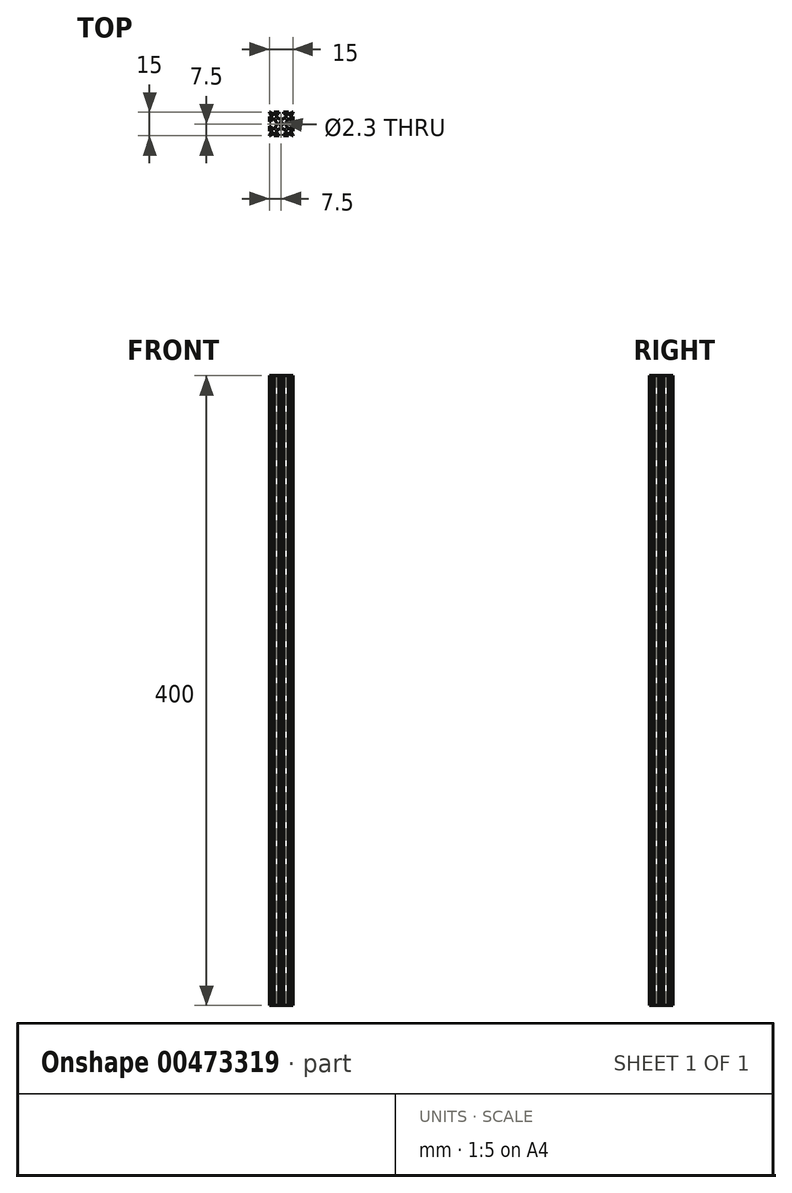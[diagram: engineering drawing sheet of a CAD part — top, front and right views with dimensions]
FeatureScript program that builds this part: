
annotation { "Feature Type Name" : "Feature", "Feature Type Description" : "" }
export const myFeature = defineFeature(function(context is Context, id is Id, definition is map)
    precondition{}
    {
        {
            var Q0;
            Q0=qCreatedBy(makeId("Top.planeOp"),FACE);
            var sketch = newSketch(context, id + "F0", { "sketchPlane" : qUnion([Q0])});
            skLineSegment(sketch, "E0", {"start": v(0, 0) * mm, "end": v(-7.5, 0) * mm, "construction": true});
            skLineSegment(sketch, "E1", {"start": v(-7.5, 1.5) * mm, "end": v(-7.5, 4.63) * mm});
            skLineSegment(sketch, "E2", {"start": v(0, 7.5) * mm, "end": v(0, 0) * mm, "construction": true});
            skArc(sketch, "E3", {"start": v(0, 1.15) * mm, "mid": v(-0.81, 0.81) * mm, "end": v(-1.15, 0) * mm});
            skLineSegment(sketch, "E4", {"start": v(0, 0) * mm, "end": v(-7.5, 7.5) * mm, "construction": true});
            skLineSegment(sketch, "E5.top", {"start": v(-7.5, 1.5) * mm, "end": v(-6.5, 1.5) * mm});
            skLineSegment(sketch, "E5.left", {"start": v(-7.5, 7.5) * mm, "end": v(-7.5, 6.8) * mm});
            skLineSegment(sketch, "E6", {"start": v(-6.5, 1.5) * mm, "end": v(-6.5, 3) * mm});
            skLineSegment(sketch, "E7", {"start": v(-6.5, 3) * mm, "end": v(-3.65, 3) * mm});
            skLineSegment(sketch, "E8", {"start": v(-3.65, 3) * mm, "end": v(-3.65, 1.5) * mm});
            skLineSegment(sketch, "E9", {"start": v(-3.65, 1.5) * mm, "end": v(-2.71, 0.81) * mm});
            skLineSegment(sketch, "E10", {"start": v(-2.71, 0.81) * mm, "end": v(-2.71, 0) * mm});
            skLineSegment(sketch, "E11", {"start": v(-7.5, 6.8) * mm, "end": v(-5.34, 4.63) * mm});
            skLineSegment(sketch, "E12", {"start": v(-5.34, 4.63) * mm, "end": v(-7.5, 4.63) * mm});
            skLineSegment(sketch, "E13.trimOffspring", {"start": v(-7.5, 4.63) * mm, "end": v(-7.5, 1.5) * mm});
            skLineSegment(sketch, "E14.trimOffspring", {"start": v(-7.5, 6.8) * mm, "end": v(-7.5, 7.5) * mm});
            skLineSegment(sketch, "E15.MirrorCS", {"start": v(-1.5, 7.5) * mm, "end": v(-4.63, 7.5) * mm});
            skLineSegment(sketch, "E16.MirrorCS", {"start": v(-7.5, 7.5) * mm, "end": v(-6.8, 7.5) * mm});
            skLineSegment(sketch, "E17.MirrorCS", {"start": v(-6.8, 7.5) * mm, "end": v(-7.5, 7.5) * mm});
            skLineSegment(sketch, "E18.MirrorCS", {"start": v(-4.63, 7.5) * mm, "end": v(-1.5, 7.5) * mm});
            skLineSegment(sketch, "E19.MirrorCS", {"start": v(-6.8, 7.5) * mm, "end": v(-4.63, 5.34) * mm});
            skLineSegment(sketch, "E20.MirrorCS", {"start": v(-3, 3.65) * mm, "end": v(-1.5, 3.65) * mm});
            skLineSegment(sketch, "E21.MirrorCS", {"start": v(-1.5, 3.65) * mm, "end": v(-0.81, 2.71) * mm});
            skLineSegment(sketch, "E22.MirrorCS", {"start": v(-3, 6.5) * mm, "end": v(-3, 3.65) * mm});
            skLineSegment(sketch, "E23.MirrorCS", {"start": v(-1.5, 7.5) * mm, "end": v(-1.5, 6.5) * mm});
            skLineSegment(sketch, "E24.MirrorCS", {"start": v(-1.5, 6.5) * mm, "end": v(-3, 6.5) * mm});
            skLineSegment(sketch, "E25.MirrorCS", {"start": v(-4.63, 5.34) * mm, "end": v(-4.63, 7.5) * mm});
            skLineSegment(sketch, "E26.MirrorCS", {"start": v(-0.81, 2.71) * mm, "end": v(0, 2.71) * mm});
            skLineSegment(sketch, "E27.MirrorCS", {"start": v(7.5, 4.63) * mm, "end": v(7.5, 1.5) * mm});
            skLineSegment(sketch, "E28.MirrorCS", {"start": v(7.5, 6.8) * mm, "end": v(7.5, 7.5) * mm});
            skLineSegment(sketch, "E29.MirrorCS", {"start": v(7.5, 7.5) * mm, "end": v(6.8, 7.5) * mm});
            skLineSegment(sketch, "E30.MirrorCS", {"start": v(4.63, 7.5) * mm, "end": v(1.5, 7.5) * mm});
            skLineSegment(sketch, "E31.MirrorCS", {"start": v(1.5, 7.5) * mm, "end": v(4.63, 7.5) * mm});
            skLineSegment(sketch, "E32.MirrorCS", {"start": v(6.8, 7.5) * mm, "end": v(7.5, 7.5) * mm});
            skLineSegment(sketch, "E33.MirrorCS", {"start": v(6.8, 7.5) * mm, "end": v(4.63, 5.34) * mm});
            skLineSegment(sketch, "E34.MirrorCS", {"start": v(1.5, 3.65) * mm, "end": v(0.81, 2.71) * mm});
            skLineSegment(sketch, "E35.MirrorCS", {"start": v(3, 6.5) * mm, "end": v(3, 3.65) * mm});
            skLineSegment(sketch, "E36.MirrorCS", {"start": v(1.5, 6.5) * mm, "end": v(3, 6.5) * mm});
            skLineSegment(sketch, "E37.MirrorCS", {"start": v(0.81, 2.71) * mm, "end": v(0, 2.71) * mm});
            skLineSegment(sketch, "E38.MirrorCS", {"start": v(7.5, 6.8) * mm, "end": v(5.34, 4.63) * mm});
            skLineSegment(sketch, "E39.MirrorCS", {"start": v(2.71, 0.81) * mm, "end": v(2.71, 0) * mm});
            skLineSegment(sketch, "E40.MirrorCS", {"start": v(3.65, 1.5) * mm, "end": v(2.71, 0.81) * mm});
            skLineSegment(sketch, "E41.MirrorCS", {"start": v(3.65, 3) * mm, "end": v(3.65, 1.5) * mm});
            skLineSegment(sketch, "E42.MirrorCS", {"start": v(6.5, 3) * mm, "end": v(3.65, 3) * mm});
            skLineSegment(sketch, "E43.MirrorCS", {"start": v(6.5, 1.5) * mm, "end": v(6.5, 3) * mm});
            skLineSegment(sketch, "E44.MirrorCS", {"start": v(7.5, 7.5) * mm, "end": v(7.5, 6.8) * mm});
            skLineSegment(sketch, "E45.MirrorCS", {"start": v(7.5, 1.5) * mm, "end": v(6.5, 1.5) * mm});
            skLineSegment(sketch, "E46.MirrorCS", {"start": v(0, 0) * mm, "end": v(7.5, 7.5) * mm, "construction": true});
            skLineSegment(sketch, "E47.MirrorCS", {"start": v(7.5, 1.5) * mm, "end": v(7.5, 4.63) * mm});
            skArc(sketch, "E48.MirrorCS", {"start": v(0, 1.15) * mm, "mid": v(0.81, 0.81) * mm, "end": v(1.15, 0) * mm});
            skLineSegment(sketch, "E49.MirrorCS", {"start": v(0, 0) * mm, "end": v(7.5, 0) * mm, "construction": true});
            skLineSegment(sketch, "E50.MirrorCS", {"start": v(5.34, 4.63) * mm, "end": v(7.5, 4.63) * mm});
            skLineSegment(sketch, "E51.MirrorCS", {"start": v(4.63, 5.34) * mm, "end": v(4.63, 7.5) * mm});
            skLineSegment(sketch, "E52.MirrorCS", {"start": v(1.5, 7.5) * mm, "end": v(1.5, 6.5) * mm});
            skLineSegment(sketch, "E53.MirrorCS", {"start": v(3, 3.65) * mm, "end": v(1.5, 3.65) * mm});
            skLineSegment(sketch, "E54.MirrorCS", {"start": v(-4.63, -7.5) * mm, "end": v(-1.5, -7.5) * mm});
            skLineSegment(sketch, "E55.MirrorCS", {"start": v(1.5, -3.65) * mm, "end": v(0.81, -2.71) * mm});
            skLineSegment(sketch, "E56.MirrorCS", {"start": v(-7.5, -4.63) * mm, "end": v(-7.5, -1.5) * mm});
            skLineSegment(sketch, "E57.MirrorCS", {"start": v(-7.5, -6.8) * mm, "end": v(-7.5, -7.5) * mm});
            skLineSegment(sketch, "E58.MirrorCS", {"start": v(7.5, -7.5) * mm, "end": v(7.5, -6.8) * mm});
            skLineSegment(sketch, "E59.MirrorCS", {"start": v(-7.5, -7.5) * mm, "end": v(-6.8, -7.5) * mm});
            skLineSegment(sketch, "E60.MirrorCS", {"start": v(7.5, -7.5) * mm, "end": v(6.8, -7.5) * mm});
            skLineSegment(sketch, "E61.MirrorCS", {"start": v(1.5, -7.5) * mm, "end": v(4.63, -7.5) * mm});
            skLineSegment(sketch, "E62.MirrorCS", {"start": v(7.5, -1.5) * mm, "end": v(7.5, -4.63) * mm});
            skLineSegment(sketch, "E63.MirrorCS", {"start": v(3.65, -3) * mm, "end": v(3.65, -1.5) * mm});
            skLineSegment(sketch, "E64.MirrorCS", {"start": v(-4.63, -5.34) * mm, "end": v(-4.63, -7.5) * mm});
            skLineSegment(sketch, "E65.MirrorCS", {"start": v(5.34, -4.63) * mm, "end": v(7.5, -4.63) * mm});
            skLineSegment(sketch, "E66.MirrorCS", {"start": v(-5.34, -4.63) * mm, "end": v(-7.5, -4.63) * mm});
            skLineSegment(sketch, "E67.MirrorCS", {"start": v(-7.5, -1.5) * mm, "end": v(-7.5, -4.63) * mm});
            skLineSegment(sketch, "E68.MirrorCS", {"start": v(0, -7.5) * mm, "end": v(0, 0) * mm, "construction": true});
            skArc(sketch, "E69.MirrorCS", {"start": v(0, -1.15) * mm, "mid": v(-0.81, -0.81) * mm, "end": v(-1.15, 0) * mm});
            skLineSegment(sketch, "E70.MirrorCS", {"start": v(0, 0) * mm, "end": v(-7.5, -7.5) * mm, "construction": true});
            skLineSegment(sketch, "E71.MirrorCS", {"start": v(-7.5, -1.5) * mm, "end": v(-6.5, -1.5) * mm});
            skLineSegment(sketch, "E72.MirrorCS", {"start": v(-7.5, -7.5) * mm, "end": v(-7.5, -6.8) * mm});
            skLineSegment(sketch, "E73.MirrorCS", {"start": v(-6.5, -1.5) * mm, "end": v(-6.5, -3) * mm});
            skLineSegment(sketch, "E74.MirrorCS", {"start": v(-6.5, -3) * mm, "end": v(-3.65, -3) * mm});
            skLineSegment(sketch, "E75.MirrorCS", {"start": v(-3.65, -3) * mm, "end": v(-3.65, -1.5) * mm});
            skLineSegment(sketch, "E76.MirrorCS", {"start": v(-3.65, -1.5) * mm, "end": v(-2.71, -0.81) * mm});
            skLineSegment(sketch, "E77.MirrorCS", {"start": v(-2.71, -0.81) * mm, "end": v(-2.71, 0) * mm});
            skLineSegment(sketch, "E78.MirrorCS", {"start": v(-7.5, -6.8) * mm, "end": v(-5.34, -4.63) * mm});
            skLineSegment(sketch, "E79.MirrorCS", {"start": v(6.5, -3) * mm, "end": v(3.65, -3) * mm});
            skLineSegment(sketch, "E80.MirrorCS", {"start": v(-0.81, -2.71) * mm, "end": v(0, -2.71) * mm});
            skLineSegment(sketch, "E81.MirrorCS", {"start": v(7.5, -6.8) * mm, "end": v(5.34, -4.63) * mm});
            skLineSegment(sketch, "E82.MirrorCS", {"start": v(-3, -6.5) * mm, "end": v(-3, -3.65) * mm});
            skLineSegment(sketch, "E83.MirrorCS", {"start": v(-6.8, -7.5) * mm, "end": v(-4.63, -5.34) * mm});
            skLineSegment(sketch, "E84.MirrorCS", {"start": v(4.63, -5.34) * mm, "end": v(4.63, -7.5) * mm});
            skLineSegment(sketch, "E85.MirrorCS", {"start": v(7.5, -6.8) * mm, "end": v(7.5, -7.5) * mm});
            skLineSegment(sketch, "E86.MirrorCS", {"start": v(3, -6.5) * mm, "end": v(3, -3.65) * mm});
            skLineSegment(sketch, "E87.MirrorCS", {"start": v(-1.5, -7.5) * mm, "end": v(-4.63, -7.5) * mm});
            skLineSegment(sketch, "E88.MirrorCS", {"start": v(6.8, -7.5) * mm, "end": v(4.63, -5.34) * mm});
            skLineSegment(sketch, "E89.MirrorCS", {"start": v(6.8, -7.5) * mm, "end": v(7.5, -7.5) * mm});
            skLineSegment(sketch, "E90.MirrorCS", {"start": v(0, 0) * mm, "end": v(7.5, -7.5) * mm, "construction": true});
            skArc(sketch, "E91.MirrorCS", {"start": v(0, -1.15) * mm, "mid": v(0.81, -0.81) * mm, "end": v(1.15, 0) * mm});
            skLineSegment(sketch, "E92.MirrorCS", {"start": v(1.5, -6.5) * mm, "end": v(3, -6.5) * mm});
            skLineSegment(sketch, "E93.MirrorCS", {"start": v(7.5, -1.5) * mm, "end": v(6.5, -1.5) * mm});
            skLineSegment(sketch, "E94.MirrorCS", {"start": v(1.5, -7.5) * mm, "end": v(1.5, -6.5) * mm});
            skLineSegment(sketch, "E95.MirrorCS", {"start": v(-3, -3.65) * mm, "end": v(-1.5, -3.65) * mm});
            skLineSegment(sketch, "E96.MirrorCS", {"start": v(-1.5, -7.5) * mm, "end": v(-1.5, -6.5) * mm});
            skLineSegment(sketch, "E97.MirrorCS", {"start": v(2.71, -0.81) * mm, "end": v(2.71, 0) * mm});
            skLineSegment(sketch, "E98.MirrorCS", {"start": v(7.5, -4.63) * mm, "end": v(7.5, -1.5) * mm});
            skLineSegment(sketch, "E99.MirrorCS", {"start": v(6.5, -1.5) * mm, "end": v(6.5, -3) * mm});
            skLineSegment(sketch, "E100.MirrorCS", {"start": v(-6.8, -7.5) * mm, "end": v(-7.5, -7.5) * mm});
            skLineSegment(sketch, "E101.MirrorCS", {"start": v(3, -3.65) * mm, "end": v(1.5, -3.65) * mm});
            skLineSegment(sketch, "E102.MirrorCS", {"start": v(4.63, -7.5) * mm, "end": v(1.5, -7.5) * mm});
            skLineSegment(sketch, "E103.MirrorCS", {"start": v(-1.5, -6.5) * mm, "end": v(-3, -6.5) * mm});
            skLineSegment(sketch, "E104.MirrorCS", {"start": v(3.65, -1.5) * mm, "end": v(2.71, -0.81) * mm});
            skLineSegment(sketch, "E105.MirrorCS", {"start": v(0.81, -2.71) * mm, "end": v(0, -2.71) * mm});
            skLineSegment(sketch, "E106.MirrorCS", {"start": v(-1.5, -3.65) * mm, "end": v(-0.81, -2.71) * mm});
            skSolve(sketch);
        }
        {
            var Q0;
            Q0=qSketchRegion(id+"F0",true);
            extrude(context, id + "F1", {"entities" : qUnion([Q0]), "depth" : 400 * mm});
        }
    });
